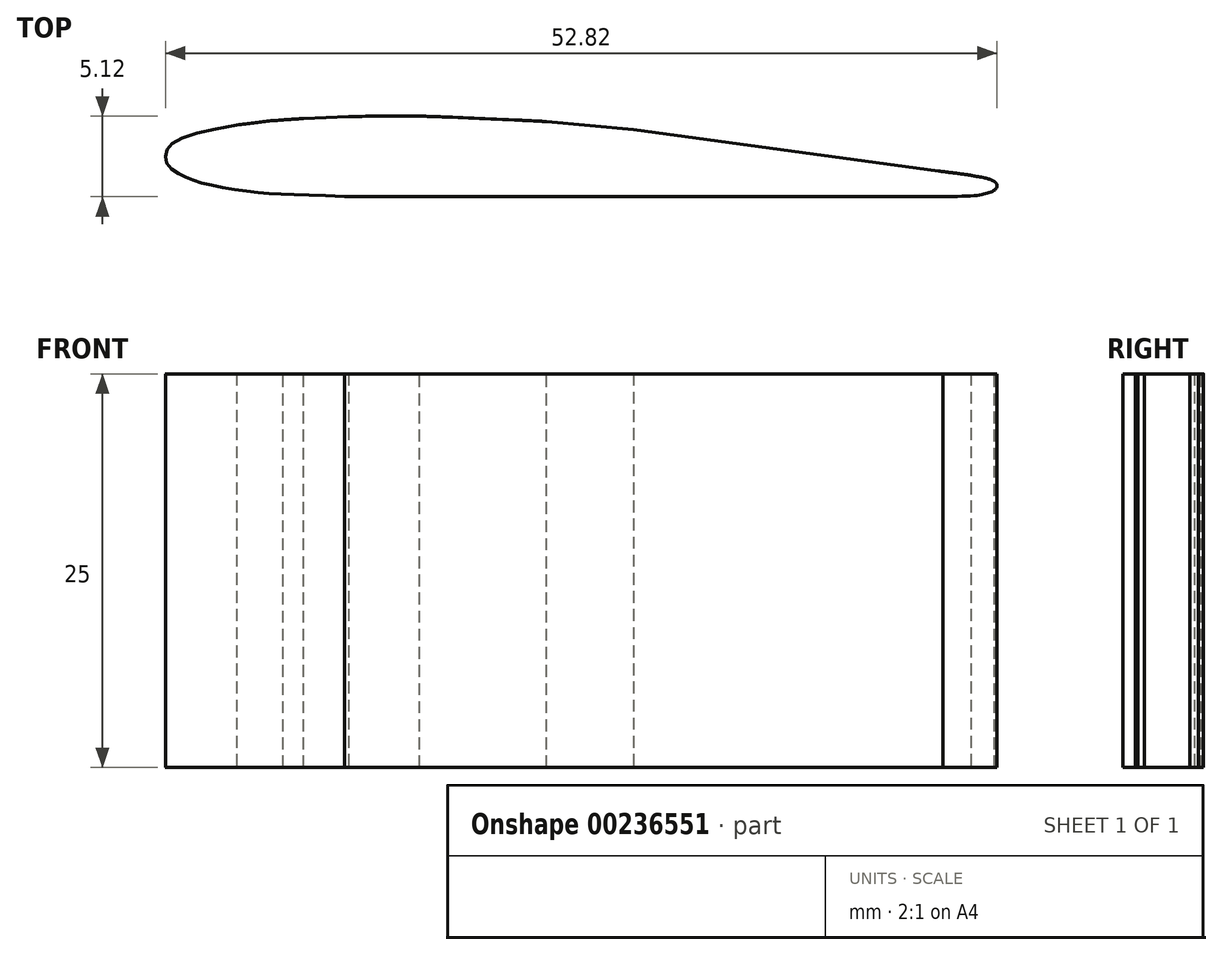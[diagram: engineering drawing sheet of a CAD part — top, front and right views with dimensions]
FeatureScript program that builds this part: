
annotation { "Feature Type Name" : "Feature", "Feature Type Description" : "" }
export const myFeature = defineFeature(function(context is Context, id is Id, definition is map)
    precondition{}
    {
        {
            var Q0;
            Q0=qCreatedBy(makeId("Top.planeOp"),FACE);
            var sketch = newSketch(context, id + "F0", { "sketchPlane" : qUnion([Q0])});
            skLineSegment(sketch, "E0", {"start": v(-29.76, 0) * mm, "end": v(20.24, 0) * mm});
            skFitSpline(sketch, "E1", {"points": [v(-20.56, 0) * mm, v(-24.53, 0.15) * mm, v(-26.56, 0.33) * mm, v(-28.8, 0.68) * mm, v(-30.2, 1.05) * mm, v(-31.1, 1.47) * mm, v(-31.85, 2.1) * mm, v(-31.9, 2.8) * mm, v(-31.14, 3.6) * mm, v(-25.61, 4.81) * mm, v(-18.35, 5.33) * mm, v(-5.32, 4.69) * mm, v(5.44, 3.5) * mm, v(17.15, 1.64) * mm, v(20.76, 0.93) * mm, v(20.93, 0.6) * mm, v(20.97, 0.43) * mm, v(20.94, 0.29) * mm, v(20.8, 0.16) * mm, v(20.6, 0) * mm, v(20.24, 0) * mm], "startDerivative": vector(-74.39, 4.38) * mm, "endDerivative": vector(-19.76, 2.89) * mm});
            skFitSpline(sketch, "E2", {"points": [v(17.44, 0) * mm, v(19.63, 0.09) * mm, v(20.16, 0.19) * mm, v(20.55, 0.33) * mm, v(20.75, 0.44) * mm, v(20.86, 0.6) * mm, v(20.87, 0.8) * mm, v(20.78, 0.92) * mm, v(20.6, 1.01) * mm, v(20.15, 1.18) * mm, v(19.24, 1.36) * mm, v(19.22, 1.36) * mm], "startDerivative": vector(11.97, 0.24) * mm, "endDerivative": vector(-4.22, -0.1) * mm});
            skLineSegment(sketch, "E3", {"start": v(-2.2, 4.26) * mm, "end": v(17.15, 1.64) * mm});
            skLineSegment(sketch, "E4", {"start": v(-7.75, 4.78) * mm, "end": v(-2.2, 4.26) * mm});
            skFitSpline(sketch, "E5", {"points": [v(-25.61, 4.81) * mm, v(-23.18, 4.97) * mm, v(-18.32, 5.17) * mm, v(-7.74, 4.78) * mm, v(-7.75, 4.78) * mm, v(-7.74, 4.78) * mm], "startDerivative": vector(11.17, 0.6) * mm, "endDerivative": vector(0.76, -0.07) * mm});
            skFitSpline(sketch, "E6.trimOffspring", {"points": [v(-20.56, 0) * mm, v(-24.53, 0.15) * mm, v(-26.56, 0.33) * mm, v(-28.8, 0.68) * mm, v(-30.2, 1.05) * mm, v(-31.1, 1.47) * mm, v(-31.85, 2.1) * mm, v(-31.9, 2.8) * mm, v(-31.14, 3.6) * mm, v(-25.61, 4.81) * mm, v(-18.35, 5.33) * mm, v(-5.32, 4.69) * mm, v(5.44, 3.5) * mm, v(17.15, 1.64) * mm, v(20.76, 0.93) * mm, v(20.93, 0.6) * mm, v(20.97, 0.43) * mm, v(20.94, 0.29) * mm, v(20.8, 0.16) * mm, v(20.6, 0) * mm, v(20.24, 0) * mm], "startDerivative": vector(-74.39, 4.38) * mm, "endDerivative": vector(-19.76, 2.89) * mm});
            skLineSegment(sketch, "E7", {"start": v(-23.18, 4.97) * mm, "end": v(-20.3, 5.09) * mm});
            skFitSpline(sketch, "E8", {"points": [v(-20.3, 5.09) * mm, v(-18.65, 5.11) * mm, v(-17.65, 5.11) * mm, v(-17.59, 5.11) * mm, v(-15.81, 5.12) * mm, v(-13.36, 5.02) * mm, v(-13.36, 5.02) * mm], "startDerivative": vector(6.97, 0.15) * mm, "endDerivative": vector(0.03, -0.13) * mm});
            skFitSpline(sketch, "E9", {"points": [v(-27.4, 4.55) * mm, v(-26.33, 4.69) * mm, v(-25.45, 4.8) * mm, v(-24.46, 4.88) * mm], "startDerivative": vector(3.16, 0.4) * mm, "endDerivative": vector(3.02, 0.23) * mm});
            skSolve(sketch);
        }
        {
            var Q0;
            {var subQ0=sQuery(id+"F0.wireOp",EDGE,"E2");var subQ1=sQuery(id+"F0.wireOp",EDGE,"E1");var subQ2=makeQuery(id+"F0.imprint","INTERSECT",VERTEX,{"disambiguationData":[OD(0.0)],"derivedFrom":[subQ1,subQ0]});Q0=makeQuery(id+"F0.imprint","IMPRINT",FACE,{"disambiguationData":[TD([[makeQuery(id+"F0.imprint","IMPRINT",EDGE,{"disambiguationData":[TD([[subQ2,1.0]])],"derivedFrom":subQ1}),1.0]])]});}
            var Q1;
            {var subQ0=sQuery(id+"F0.wireOp",EDGE,"b6JS9hz3-AJ0V-WIle-FYZ6-CmjX2AeKnGu5");var subQ1=sQuery(id+"F0.wireOp",EDGE,"E1");var subQ2=makeQuery(id+"F0.imprint","INTERSECT",VERTEX,{"derivedFrom":[subQ1,subQ0]});Q1=makeQuery(id+"F0.imprint","IMPRINT",FACE,{"disambiguationData":[TD([[makeQuery(id+"F0.imprint","IMPRINT",EDGE,{"disambiguationData":[TD([[subQ2,-1.0]])],"derivedFrom":subQ1}),-1.0]])]});}
            var Q2;
            {var subQ1=sQuery(id+"F0.wireOp",EDGE,"E1");var subQ6=sQuery(id+"F0.wireOp",EDGE,"E0");var subQ7=makeQuery(id+"F0.imprint","INTERSECT",VERTEX,{"derivedFrom":[subQ6,subQ1]});Q2=makeQuery(id+"F0.imprint","IMPRINT",FACE,{"disambiguationData":[TD([[makeQuery(id+"F0.imprint","IMPRINT",EDGE,{"disambiguationData":[TD([[subQ7,-1.0]])],"derivedFrom":subQ6}),1.0]])]});}
            extrude(context, id + "F1", {"entities" : qUnion([Q0, Q1, Q2]), "depth" : 25 * mm});
        }
    });
